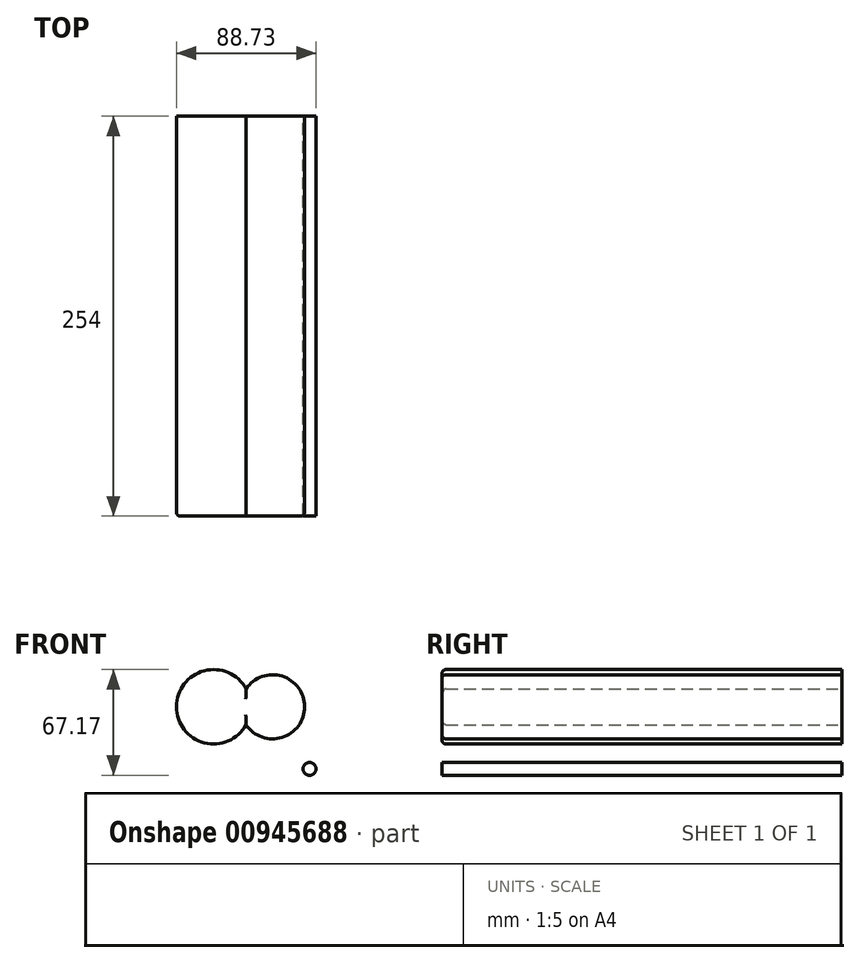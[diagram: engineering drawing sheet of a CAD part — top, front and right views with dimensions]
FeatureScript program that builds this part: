
annotation { "Feature Type Name" : "Feature", "Feature Type Description" : "" }
export const myFeature = defineFeature(function(context is Context, id is Id, definition is map)
    precondition{}
    {
        {
            var Q0;
            Q0=qCreatedBy(makeId("Front.planeOp"),FACE);
            var sketch = newSketch(context, id + "F0", { "sketchPlane" : qUnion([Q0])});
            skCircle(sketch, "E0", {"center": v(0, 0) * mm, "radius": 20.35 * mm});
            skCircle(sketch, "E1", {"center": v(-37.51, 0) * mm, "radius": 23.64 * mm});
            skCircle(sketch, "E2", {"center": v(23.48, -39.45) * mm, "radius": 4.09 * mm});
            skSolve(sketch);
        }
        {
            var Q0;
            Q0 = qSketchRegion(id + "F0", true);
            extrude(context, id + "F1", {"entities" : qUnion([Q0]), "depth" : 254 * mm, "offsetDistance" : 25.4 * mm});
        }
        {
            var Q0;
            Q0=makeQuery(id+"F1.opExtrude","CAP_EDGE",EDGE,{"disambiguationData":[OSD([sQuery(id+"F0.wireOp",EDGE,"E1")])],"isStart":false});
            var Q1;
            Q1=makeQuery(id+"F1.opExtrude","CAP_EDGE",EDGE,{"disambiguationData":[OSD([sQuery(id+"F0.wireOp",EDGE,"E0")])],"isStart":false});
            fillet(context, id + "F2", {"entities" : qUnion([Q0, Q1]), "radius" : 2.54 * mm, "tangentPropagation" : true, "allowEdgeOverflow" : false});
        }
    });
